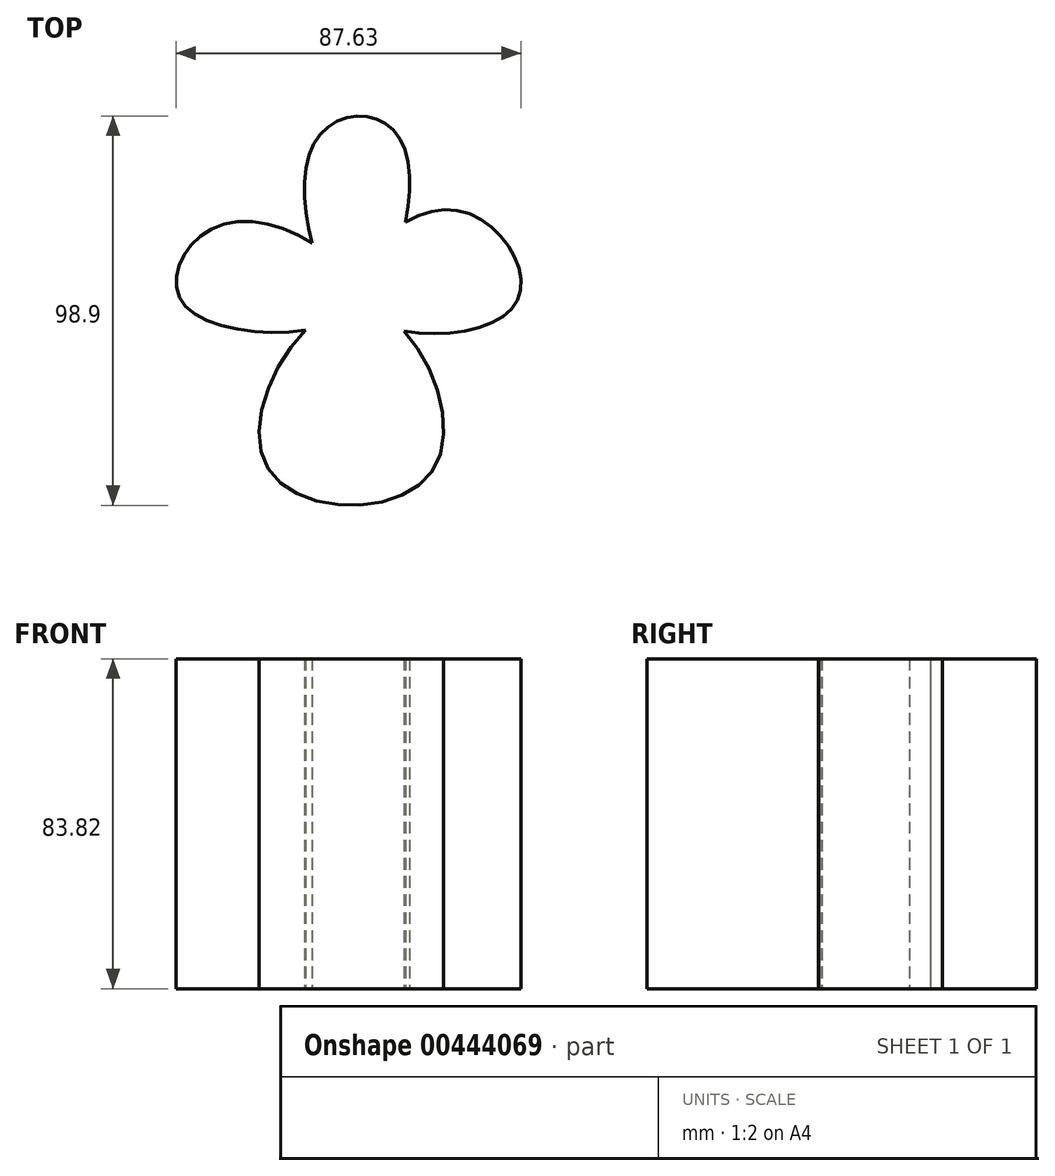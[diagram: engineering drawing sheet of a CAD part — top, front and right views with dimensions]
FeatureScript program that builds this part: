
annotation { "Feature Type Name" : "Feature", "Feature Type Description" : "" }
export const myFeature = defineFeature(function(context is Context, id is Id, definition is map)
    precondition{}
    {
        {
            var Q0;
            Q0=qCreatedBy(makeId("Top.planeOp"),FACE);
            var sketch = newSketch(context, id + "F0", { "sketchPlane" : qUnion([Q0])});
            skFitSpline(sketch, "E0", {"points": [v(0, 0) * mm, v(23.83, 24.4) * mm, v(40, 0) * mm, v(0, 0) * mm]});
            skSolve(sketch);
        }
        {
            var Q0;
            Q0=makeQuery(id+"F0.imprint","IMPRINT",FACE,{"disambiguationData":[TD([[makeQuery(id+"F0.imprint","IMPRINT",EDGE,{"derivedFrom":sQuery(id+"F0.wireOp",EDGE,"E0")}),-1.0]])]});
            extrude(context, id + "F1", {"entities" : qUnion([Q0]), "depth" : 83.82 * mm});
        }
        {
            var Q0;
            Q0=qCreatedBy(makeId("Top.planeOp"),FACE);
            var sketch = newSketch(context, id + "F2", { "sketchPlane" : qUnion([Q0])});
            skFitSpline(sketch, "E1", {"points": [v(0, 0) * mm, v(-31.2, 21.28) * mm, v(-43.7, 0) * mm, v(0, 0) * mm]});
            skSolve(sketch);
        }
        {
            var Q0;
            Q0=makeQuery(id+"F2.imprint","IMPRINT",FACE,{"disambiguationData":[TD([[makeQuery(id+"F2.imprint","IMPRINT",EDGE,{"derivedFrom":sQuery(id+"F2.wireOp",EDGE,"E1")}),1.0]])]});
            extrude(context, id + "F3", {"entities" : qUnion([Q0]), "operationType" : NewBodyOperationType.ADD, "depth" : 83.82 * mm});
        }
        {
            var Q0;
            Q0=qCreatedBy(makeId("Top.planeOp"),FACE);
            var sketch = newSketch(context, id + "F4", { "sketchPlane" : qUnion([Q0])});
            skFitSpline(sketch, "E2", {"points": [v(0, 0) * mm, v(-11.07, 40.86) * mm, v(11.07, 42.27) * mm, v(0, 0) * mm]});
            skSolve(sketch);
        }
        {
            var Q0;
            Q0=makeQuery(id+"F4.imprint","IMPRINT",FACE,{"disambiguationData":[TD([[makeQuery(id+"F4.imprint","IMPRINT",EDGE,{"derivedFrom":sQuery(id+"F4.wireOp",EDGE,"E2")}),-1.0]])]});
            extrude(context, id + "F5", {"entities" : qUnion([Q0]), "operationType" : NewBodyOperationType.ADD, "depth" : 83.82 * mm});
        }
        {
            var Q0;
            Q0=qCreatedBy(makeId("Top.planeOp"),FACE);
            var sketch = newSketch(context, id + "F6", { "sketchPlane" : qUnion([Q0])});
            skFitSpline(sketch, "E3", {"points": [v(0, 0) * mm, v(-22.98, -40.57) * mm, v(19.58, -41.42) * mm, v(0, 0) * mm]});
            skSolve(sketch);
        }
        {
            var Q0;
            Q0=makeQuery(id+"F6.imprint","IMPRINT",FACE,{"disambiguationData":[TD([[makeQuery(id+"F6.imprint","IMPRINT",EDGE,{"derivedFrom":sQuery(id+"F6.wireOp",EDGE,"E3")}),1.0]])]});
            extrude(context, id + "F7", {"entities" : qUnion([Q0]), "operationType" : NewBodyOperationType.ADD, "depth" : 83.82 * mm});
        }
    });
